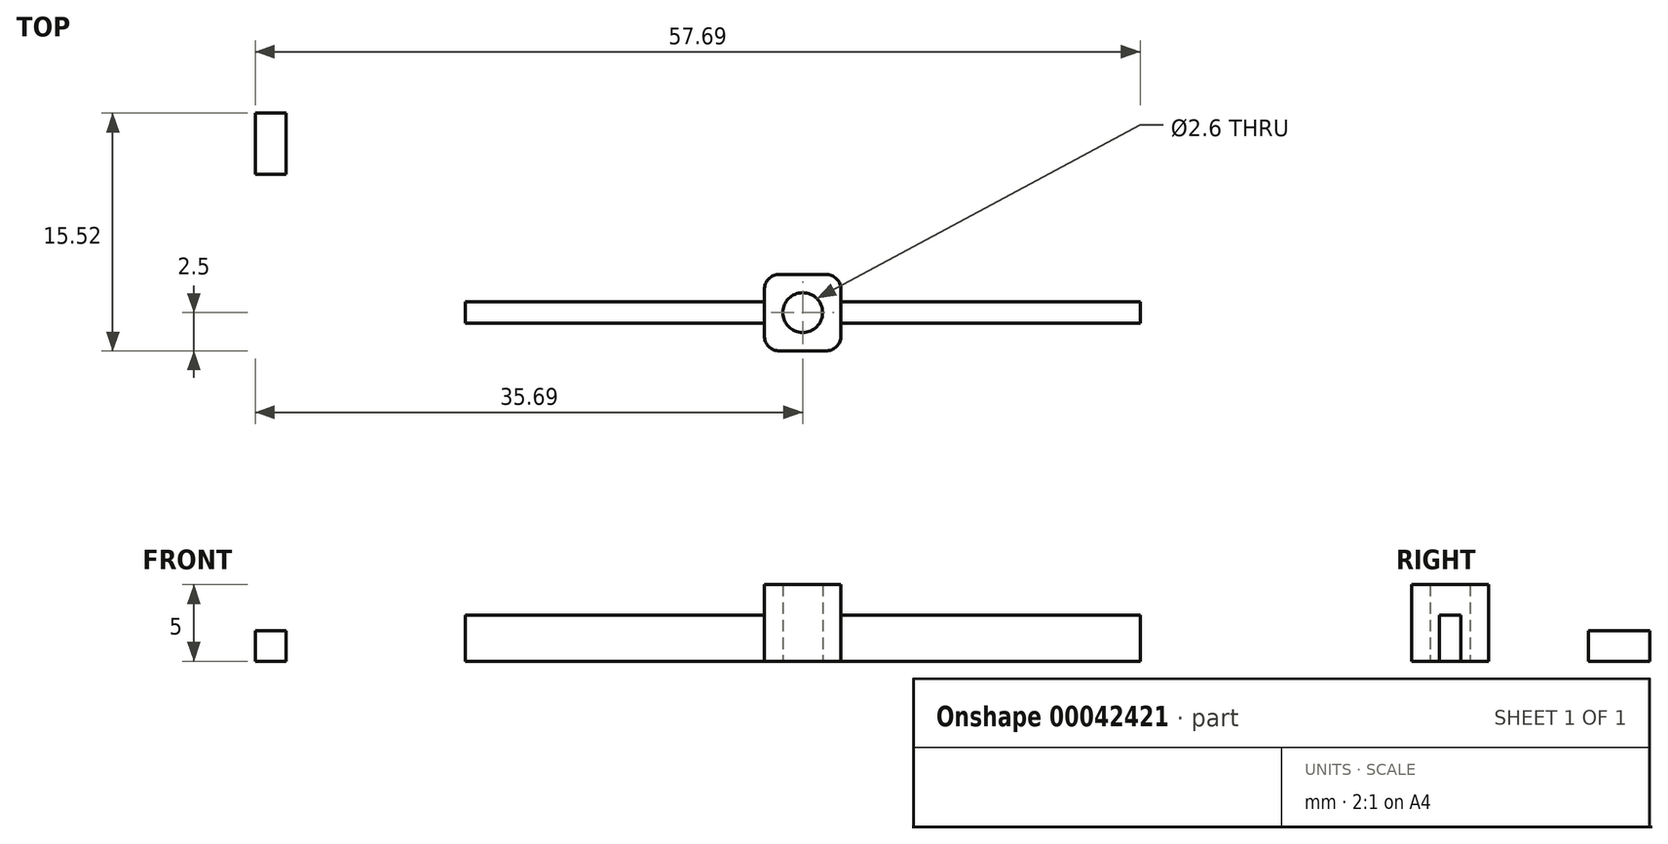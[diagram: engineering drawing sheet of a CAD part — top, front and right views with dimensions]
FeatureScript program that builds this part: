
annotation { "Feature Type Name" : "Feature", "Feature Type Description" : "" }
export const myFeature = defineFeature(function(context is Context, id is Id, definition is map)
    precondition{}
    {
        {
            var Q0;
            Q0=qCreatedBy(makeId("Top.planeOp"),FACE);
            var sketch = newSketch(context, id + "F0", { "sketchPlane" : qUnion([Q0])});
            skLineSegment(sketch, "E0.rect.bottom", {"start": v(-22, 0.7) * mm, "end": v(22, 0.7) * mm});
            skLineSegment(sketch, "E0.rect.top", {"start": v(-22, -0.7) * mm, "end": v(22, -0.7) * mm});
            skLineSegment(sketch, "E0.rect.left", {"start": v(-22, 0.7) * mm, "end": v(-22, -0.7) * mm});
            skLineSegment(sketch, "E0.rect.right", {"start": v(22, 0.7) * mm, "end": v(22, -0.7) * mm});
            skPoint(sketch, "E0.rect.middle", {"position": v(0, 0) * mm});
            skLineSegment(sketch, "E1.rect.bottom", {"start": v(-1.5, 2.5) * mm, "end": v(1.5, 2.5) * mm});
            skLineSegment(sketch, "E1.rect.top", {"start": v(-1.5, -2.5) * mm, "end": v(1.5, -2.5) * mm});
            skLineSegment(sketch, "E1.rect.left", {"start": v(-2.5, 1.5) * mm, "end": v(-2.5, -1.5) * mm});
            skLineSegment(sketch, "E1.rect.right", {"start": v(2.5, 1.5) * mm, "end": v(2.5, -1.5) * mm});
            skPoint(sketch, "E2.visualSharp", {"position": v(-2.5, 2.5) * mm});
            skArc(sketch, "E2.filletArc", {"start": v(-1.5, 2.5) * mm, "mid": v(-2.2, 2.2) * mm, "end": v(-2.5, 1.5) * mm});
            skPoint(sketch, "E3.visualSharp", {"position": v(-2.5, -2.5) * mm});
            skArc(sketch, "E3.filletArc", {"start": v(-2.5, -1.5) * mm, "mid": v(-2.2, -2.2) * mm, "end": v(-1.5, -2.5) * mm});
            skPoint(sketch, "E4.visualSharp", {"position": v(2.5, 2.5) * mm});
            skArc(sketch, "E4.filletArc", {"start": v(2.5, 1.5) * mm, "mid": v(2.2, 2.2) * mm, "end": v(1.5, 2.5) * mm});
            skPoint(sketch, "E5.visualSharp", {"position": v(2.5, -2.5) * mm});
            skArc(sketch, "E5.filletArc", {"start": v(1.5, -2.5) * mm, "mid": v(2.2, -2.2) * mm, "end": v(2.5, -1.5) * mm});
            skCircle(sketch, "E6", {"center": v(0, 0) * mm, "radius": 1.3 * mm});
            skLineSegment(sketch, "E7.bottom", {"start": v(-35.7, 13.02) * mm, "end": v(-33.7, 13.02) * mm});
            skLineSegment(sketch, "E7.top", {"start": v(-35.7, 9.02) * mm, "end": v(-33.7, 9.02) * mm});
            skLineSegment(sketch, "E7.left", {"start": v(-35.7, 13.02) * mm, "end": v(-35.7, 9.02) * mm});
            skLineSegment(sketch, "E7.right", {"start": v(-33.7, 13.02) * mm, "end": v(-33.7, 9.02) * mm});
            skSolve(sketch);
        }
        {
            var Q0;
            {var subQ5=sQuery(id+"F0.wireOp",EDGE,"E0.rect.left");Q0=makeQuery(id+"F0.imprint","IMPRINT",FACE,{"disambiguationData":[TD([[makeQuery(id+"F0.imprint","IMPRINT",EDGE,{"derivedFrom":subQ5}),1.0]])]});}
            var Q1;
            {var subQ5=sQuery(id+"F0.wireOp",EDGE,"E0.rect.right");Q1=makeQuery(id+"F0.imprint","IMPRINT",FACE,{"disambiguationData":[TD([[makeQuery(id+"F0.imprint","IMPRINT",EDGE,{"derivedFrom":subQ5}),-1.0]])]});}
            extrude(context, id + "F1", {"entities" : qUnion([Q0, Q1]), "depth" : 3 * mm});
        }
        {
            var Q0;
            Q0=makeQuery(id+"F0.imprint","IMPRINT",FACE,{"disambiguationData":[TD([[makeQuery(id+"F0.imprint","IMPRINT",EDGE,{"derivedFrom":sQuery(id+"F0.wireOp",EDGE,"E1.rect.bottom")}),-1.0]])]});
            var Q1;
            {var subQ3=sQuery(id+"F0.wireOp",EDGE,"E0.rect.bottom");var subQ5=sQuery(id+"F0.wireOp",EDGE,"E1.rect.left");var subQ7=makeQuery(id+"F0.imprint","INTERSECT",VERTEX,{"derivedFrom":[subQ3,subQ5]});Q1=makeQuery(id+"F0.imprint","IMPRINT",FACE,{"disambiguationData":[TD([[makeQuery(id+"F0.imprint","IMPRINT",EDGE,{"disambiguationData":[TD([[subQ7,-1.0]])],"derivedFrom":subQ3}),-1.0]])]});}
            var Q2;
            {var subQ3=sQuery(id+"F0.wireOp",EDGE,"E0.rect.bottom");var subQ5=sQuery(id+"F0.wireOp",EDGE,"E1.rect.right");var subQ7=makeQuery(id+"F0.imprint","INTERSECT",VERTEX,{"derivedFrom":[subQ3,subQ5]});Q2=makeQuery(id+"F0.imprint","IMPRINT",FACE,{"disambiguationData":[TD([[makeQuery(id+"F0.imprint","IMPRINT",EDGE,{"disambiguationData":[TD([[subQ7,1.0]])],"derivedFrom":subQ3}),-1.0]])]});}
            var Q3;
            Q3=makeQuery(id+"F0.imprint","IMPRINT",FACE,{"disambiguationData":[TD([[makeQuery(id+"F0.imprint","IMPRINT",EDGE,{"derivedFrom":sQuery(id+"F0.wireOp",EDGE,"E1.rect.top")}),1.0]])]});
            extrude(context, id + "F2", {"entities" : qUnion([Q0, Q1, Q2, Q3]), "depth" : 5 * mm});
        }
        {
            var Q0;
            Q0=makeQuery(id+"F0.imprint","IMPRINT",FACE,{"disambiguationData":[TD([[makeQuery(id+"F0.imprint","IMPRINT",EDGE,{"derivedFrom":sQuery(id+"F0.wireOp",EDGE,"E7.bottom")}),-1.0]])]});
            extrude(context, id + "F3", {"entities" : qUnion([Q0]), "depth" : 2 * mm});
        }
    });
